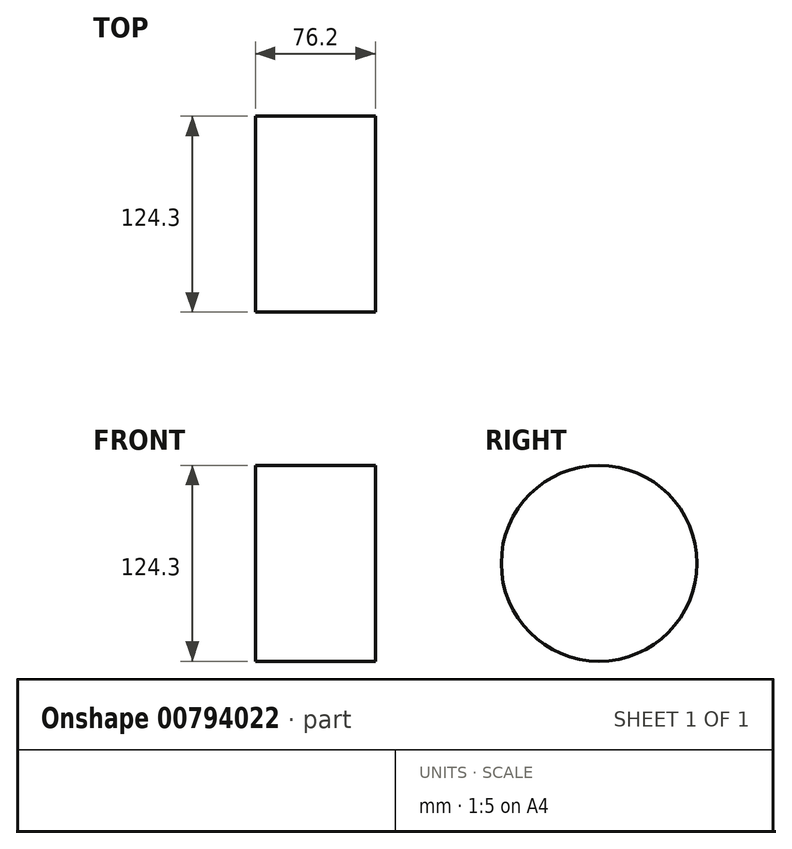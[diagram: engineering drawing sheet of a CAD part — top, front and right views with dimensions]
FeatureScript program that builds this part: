
annotation { "Feature Type Name" : "Feature", "Feature Type Description" : "" }
export const myFeature = defineFeature(function(context is Context, id is Id, definition is map)
    precondition{}
    {
        {
            var Q0;
            Q0=qCreatedBy(makeId("Right.planeOp"),FACE);
            var sketch = newSketch(context, id + "F0", { "sketchPlane" : qUnion([Q0])});
            skCircle(sketch, "E0", {"center": v(-23.75, 32.67) * mm, "radius": 62.15 * mm});
            skSolve(sketch);
        }
        {
            var Q0;
            Q0=makeQuery(id+"F0.imprint","IMPRINT",FACE,{"disambiguationData":[TD([[makeQuery(id+"F0.imprint","IMPRINT",EDGE,{"derivedFrom":sQuery(id+"F0.wireOp",EDGE,"E0")}),1.0]])]});
            extrude(context, id + "F1", {"entities" : qUnion([Q0]), "depth" : 76.2 * mm, "offsetDistance" : 25.4 * mm});
        }
    });
